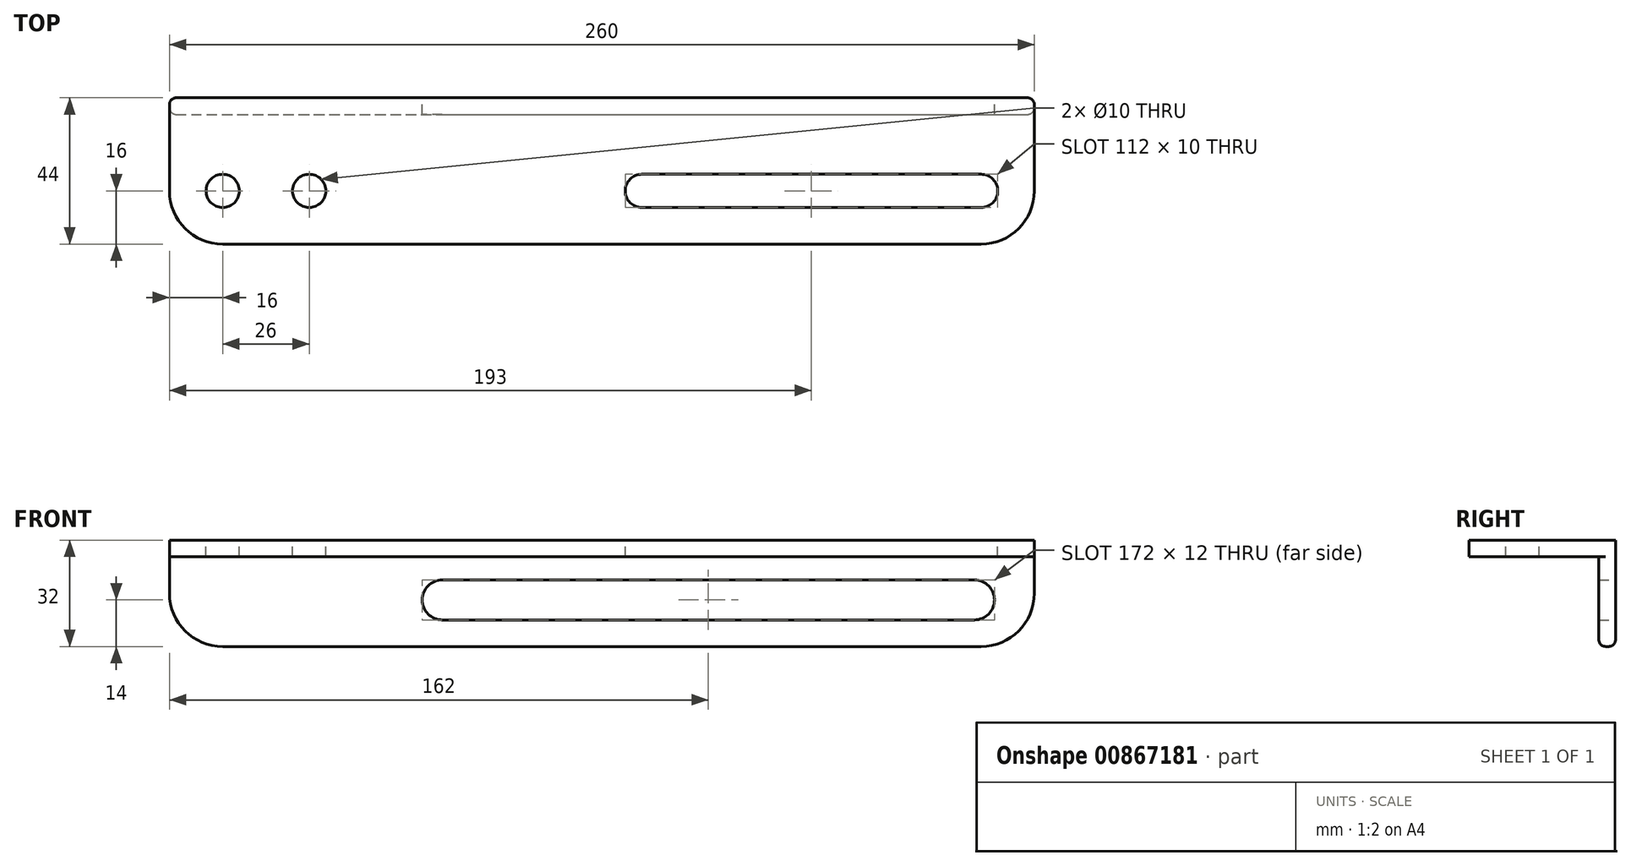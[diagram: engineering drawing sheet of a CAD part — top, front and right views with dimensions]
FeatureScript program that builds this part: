
annotation { "Feature Type Name" : "Feature", "Feature Type Description" : "" }
export const myFeature = defineFeature(function(context is Context, id is Id, definition is map)
    precondition{}
    {
        {
            var Q0;
            Q0=qCreatedBy(makeId("Top.planeOp"),FACE);
            var sketch = newSketch(context, id + "F0", { "sketchPlane" : qUnion([Q0])});
            skLineSegment(sketch, "E0", {"start": v(130, 0) * mm, "end": v(-130, 0) * mm});
            skLineSegment(sketch, "E1", {"start": v(130, 0) * mm, "end": v(130, -28) * mm});
            skLineSegment(sketch, "E2", {"start": v(114, -44) * mm, "end": v(-114, -44) * mm});
            skLineSegment(sketch, "E3", {"start": v(-130, -28) * mm, "end": v(-130, 0) * mm});
            skPoint(sketch, "E4.visualSharp", {"position": v(130, -44) * mm});
            skArc(sketch, "E4.filletArc", {"start": v(114, -44) * mm, "mid": v(125.31, -39.31) * mm, "end": v(130, -28) * mm});
            skPoint(sketch, "E5.visualSharp", {"position": v(-130, -44) * mm});
            skArc(sketch, "E5.filletArc", {"start": v(-130, -28) * mm, "mid": v(-125.31, -39.31) * mm, "end": v(-114, -44) * mm});
            skLineSegment(sketch, "E6", {"start": v(-145.87, -28) * mm, "end": v(164.12, -28) * mm, "construction": true});
            skLineSegment(sketch, "E7", {"start": v(114, -10.01) * mm, "end": v(114, -55.36) * mm, "construction": true});
            skLineSegment(sketch, "E8", {"start": v(12, -13.1) * mm, "end": v(12, -54.27) * mm, "construction": true});
            skLineSegment(sketch, "E9", {"start": v(114, -23) * mm, "end": v(12, -23) * mm});
            skLineSegment(sketch, "E10.MirrorCS", {"start": v(114, -33) * mm, "end": v(12, -33) * mm});
            skArc(sketch, "E11", {"start": v(12, -33) * mm, "mid": v(7, -28) * mm, "end": v(12, -23) * mm});
            skPoint(sketch, "E11.centerSnap0", {"position": v(9.13, -28) * mm});
            skArc(sketch, "E12", {"start": v(114, -23) * mm, "mid": v(119, -28) * mm, "end": v(114, -33) * mm});
            skCircle(sketch, "E13", {"center": v(-114, -28) * mm, "radius": 5 * mm});
            skLineSegment(sketch, "E14", {"start": v(-88, -36.86) * mm, "end": v(-88, -17.9) * mm, "construction": true});
            skCircle(sketch, "E15", {"center": v(-88, -28) * mm, "radius": 5 * mm});
            skSolve(sketch);
        }
        {
            var Q0;
            Q0=makeQuery(id+"F0.imprint","IMPRINT",FACE,{"disambiguationData":[TD([[makeQuery(id+"F0.imprint","IMPRINT",EDGE,{"derivedFrom":sQuery(id+"F0.wireOp",EDGE,"E0")}),1.0]])]});
            extrude(context, id + "F1", {"entities" : qUnion([Q0]), "oppositeDirection" : true, "depth" : 5 * mm, "offsetDistance" : 25 * mm});
        }
        {
            var Q0;
            Q0=makeQuery(id+"F1.opExtrude","CAP_FACE",FACE,{"disambiguationData":[OSD([sQuery(id+"F0.wireOp",EDGE,"E0"),sQuery(id+"F0.wireOp",EDGE,"E1"),sQuery(id+"F0.wireOp",EDGE,"E2"),sQuery(id+"F0.wireOp",EDGE,"E3"),sQuery(id+"F0.wireOp",EDGE,"E4.filletArc"),sQuery(id+"F0.wireOp",EDGE,"E5.filletArc"),sQuery(id+"F0.wireOp",EDGE,"E9"),sQuery(id+"F0.wireOp",EDGE,"E10.MirrorCS"),sQuery(id+"F0.wireOp",EDGE,"E11"),sQuery(id+"F0.wireOp",EDGE,"E12"),sQuery(id+"F0.wireOp",EDGE,"E13"),sQuery(id+"F0.wireOp",EDGE,"E15")])],"isStart":false});
            var sketch = newSketch(context, id + "F2", { "sketchPlane" : qUnion([Q0])});
            skLineSegment(sketch, "E16", {"start": v(130, 0) * mm, "end": v(-130, 0) * mm});
            skLineSegment(sketch, "E17", {"start": v(-130, 0) * mm, "end": v(-130, 5) * mm});
            skLineSegment(sketch, "E18", {"start": v(-130, 5) * mm, "end": v(130, 5) * mm});
            skLineSegment(sketch, "E19", {"start": v(130, 5) * mm, "end": v(130, 0) * mm});
            skSolve(sketch);
        }
        {
            var Q0;
            Q0=makeQuery(id+"F2.imprint","IMPRINT",FACE,{"disambiguationData":[TD([[makeQuery(id+"F2.imprint","IMPRINT",EDGE,{"derivedFrom":sQuery(id+"F2.wireOp",EDGE,"E16")}),-1.0]])]});
            extrude(context, id + "F3", {"entities" : qUnion([Q0]), "operationType" : NewBodyOperationType.ADD, "depth" : 27 * mm, "offsetDistance" : 25 * mm});
        }
        {
            var Q0;
            Q0=makeQuery(id+"F3.opExtrude","CAP_EDGE",EDGE,{"disambiguationData":[OSD([sQuery(id+"F2.wireOp",EDGE,"E19")])],"isStart":false});
            var Q1;
            Q1=makeQuery(id+"F3.opExtrude","CAP_EDGE",EDGE,{"disambiguationData":[OSD([sQuery(id+"F2.wireOp",EDGE,"E17")])],"isStart":false});
            fillet(context, id + "F4", {"entities" : qUnion([Q0, Q1]), "radius" : 16 * mm, "tangentPropagation" : true, "allowEdgeOverflow" : false});
        }
        {
            var Q0;
            Q0=makeQuery(id+"F3.boolean.opBoolean","MERGE",FACE,{"derivedFrom":[makeQuery(id+"F1.opExtrude","SWEPT_FACE",FACE,{"disambiguationData":[OSD([sQuery(id+"F0.wireOp",EDGE,"E0")])]}),makeQuery(id+"F3.opExtrude","SWEPT_FACE",FACE,{"disambiguationData":[OSD([sQuery(id+"F2.wireOp",EDGE,"E16")])]})]});
            var sketch = newSketch(context, id + "F5", { "sketchPlane" : qUnion([Q0])});
            skLineSegment(sketch, "E20", {"start": v(-229.99, -18) * mm, "end": v(234.6, -18) * mm, "construction": true});
            skLineSegment(sketch, "E21", {"start": v(-112, 7.3) * mm, "end": v(-112, -40.6) * mm, "construction": true});
            skLineSegment(sketch, "E22", {"start": v(48, 7.6) * mm, "end": v(48, -41.5) * mm, "construction": true});
            skLineSegment(sketch, "E23", {"start": v(48, -12) * mm, "end": v(-112, -12) * mm});
            skLineSegment(sketch, "E24.MirrorCS", {"start": v(48, -24) * mm, "end": v(-112, -24) * mm});
            skArc(sketch, "E25", {"start": v(-112, -12) * mm, "mid": v(-118, -18) * mm, "end": v(-112, -24) * mm});
            skArc(sketch, "E26", {"start": v(48, -12) * mm, "mid": v(54, -18) * mm, "end": v(48, -24) * mm});
            skSolve(sketch);
        }
        {
            var Q0;
            Q0=makeQuery(id+"F5.imprint","IMPRINT",FACE,{"disambiguationData":[TD([[makeQuery(id+"F5.imprint","IMPRINT",EDGE,{"derivedFrom":sQuery(id+"F5.wireOp",EDGE,"E23")}),1.0]])]});
            extrude(context, id + "F6", {"entities" : qUnion([Q0]), "operationType" : NewBodyOperationType.REMOVE, "oppositeDirection" : true, "depth" : 5 * mm, "offsetDistance" : 25 * mm});
        }
        {
            var Q0;
            Q0=makeQuery(id+"F3.opExtrude","CAP_EDGE",EDGE,{"disambiguationData":[OSD([sQuery(id+"F2.wireOp",EDGE,"E16")])],"isStart":false});
            var Q1;
            Q1=makeQuery(id+"F4.opFillet","BLEND_EDGE",EDGE,{"blendedFrom":[makeQuery(id+"F3.opExtrude","CAP_EDGE",EDGE,{"disambiguationData":[OSD([sQuery(id+"F2.wireOp",EDGE,"E17")])],"isStart":false}),makeQuery(id+"F3.opExtrude","SWEPT_FACE",FACE,{"disambiguationData":[OSD([sQuery(id+"F2.wireOp",EDGE,"E18")])]})],"blendedInto":[makeQuery(id+"F3.opExtrude","SWEPT_FACE",FACE,{"disambiguationData":[OSD([sQuery(id+"F2.wireOp",EDGE,"E18")])]})]});
            var Q2;
            Q2=makeQuery(id+"F3.opExtrude","CAP_EDGE",EDGE,{"disambiguationData":[OSD([sQuery(id+"F2.wireOp",EDGE,"E18")])],"isStart":true});
            fillet(context, id + "F7", {"entities" : qUnion([Q0, Q1, Q2]), "radius" : 2 * mm, "tangentPropagation" : true, "allowEdgeOverflow" : false});
        }
    });
